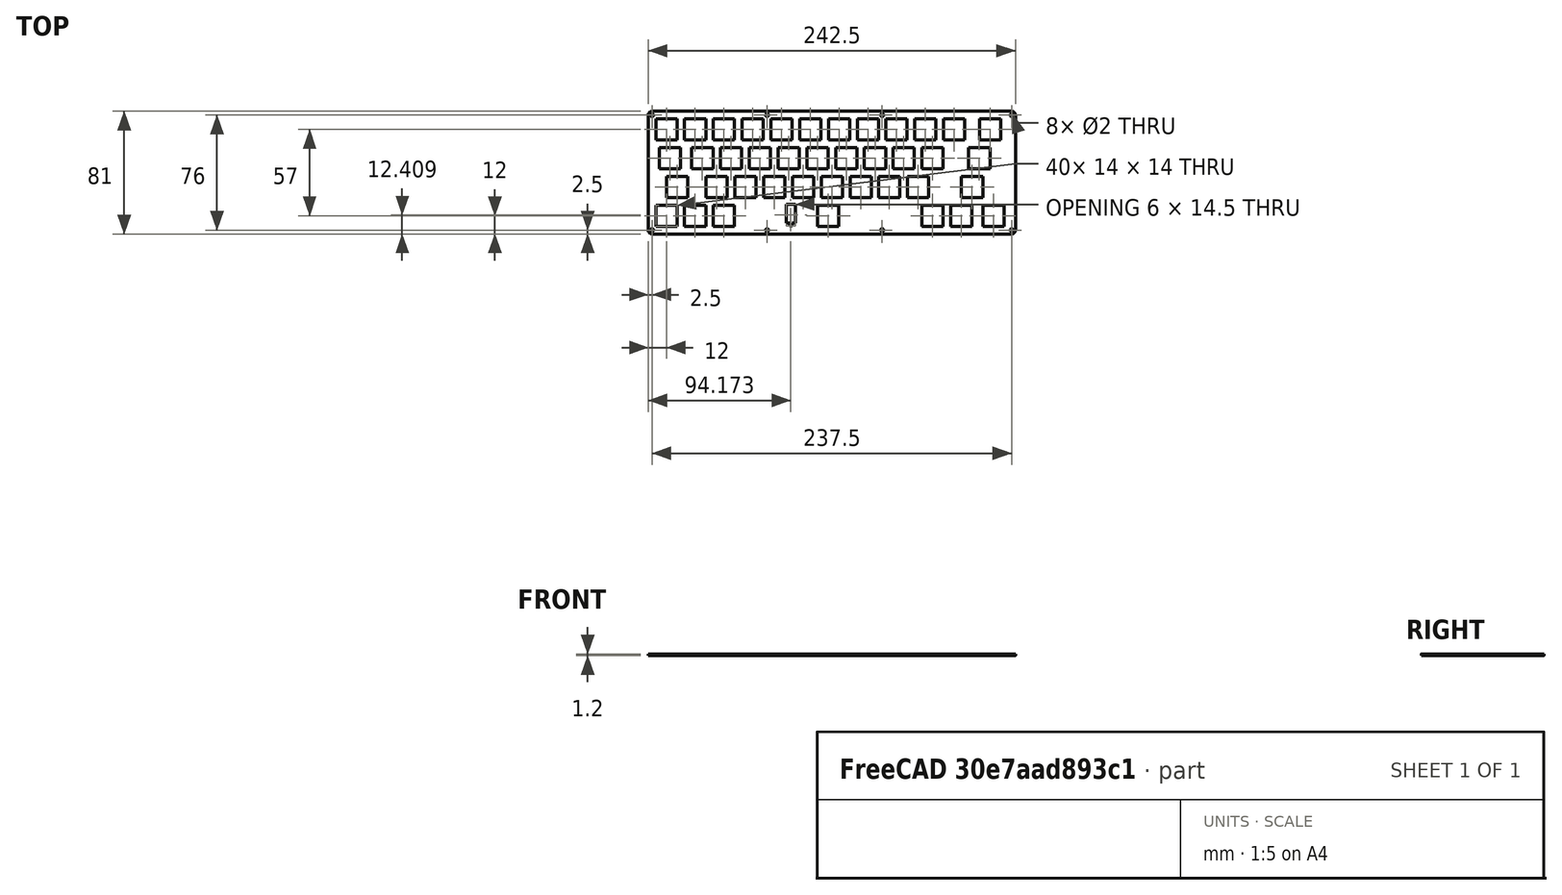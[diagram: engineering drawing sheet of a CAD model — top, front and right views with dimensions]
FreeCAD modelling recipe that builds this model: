
FCSTD DOCUMENT  (FreeCAD 1.0R39285 (Git))
Label: keys-plate
License: All rights reserved
LicenseURL: https://en.wikipedia.org/wiki/All_rights_reserved
objects: Sketcher::SketchObject×2, PartDesign::Pad×1, PartDesign::Body×1
note: 8 computed .brp shape members not serialized (recipe doc carries the construction recipe); baked Part::Feature solids carry a one-line shape summary decoded from their .brp

FEATURE [Sketcher::SketchObject] Sketch
  ArcFitTolerance = 1e-06
  FullyConstrained = true
  MakeInternals = false
FEATURE [Sketcher::SketchObject] Sketch001
  ArcFitTolerance = 1e-06
  AttachmentSupport = -> [XY_Plane]
  FullyConstrained = false
  MakeInternals = false
  MapMode = 5
  sketch-geometry (184):
    g0: LineSegment StartX=-121.25 StartY=-38 StartZ=0 EndX=-121.25 EndY=38 EndZ=0
    g1: ArcOfCircle CenterX=-118.75 CenterY=38 CenterZ=0 NormalX=0 NormalY=0 NormalZ=1 AngleXU=0 Radius=2.5 StartAngle=1.5708 EndAngle=3.14159
    g2: LineSegment StartX=-118.75 StartY=40.5 StartZ=0 EndX=118.75 EndY=40.5 EndZ=0
    g3: ArcOfCircle CenterX=118.75 CenterY=38 CenterZ=0 NormalX=0 NormalY=0 NormalZ=1 AngleXU=0 Radius=2.5 StartAngle=4e-16 EndAngle=1.5708
    g4: LineSegment StartX=121.25 StartY=38 StartZ=0 EndX=121.25 EndY=-38 EndZ=0
    g5: ArcOfCircle CenterX=118.75 CenterY=-38 CenterZ=0 NormalX=0 NormalY=0 NormalZ=1 AngleXU=0 Radius=2.5 StartAngle=4.71239 EndAngle=6.28319
    g6: LineSegment StartX=118.75 StartY=-40.5 StartZ=0 EndX=-118.75 EndY=-40.5 EndZ=0
    g7: ArcOfCircle CenterX=-118.75 CenterY=-38 CenterZ=0 NormalX=0 NormalY=0 NormalZ=1 AngleXU=0 Radius=2.5 StartAngle=3.14159 EndAngle=4.71239
    g8: Circle CenterX=-118.75 CenterY=38 CenterZ=0 NormalX=0 NormalY=0 NormalZ=1 AngleXU=0 Radius=1
    g9: Circle CenterX=-42.75 CenterY=38 CenterZ=0 NormalX=0 NormalY=0 NormalZ=1 AngleXU=0 Radius=1
    g10: Circle CenterX=33.25 CenterY=38 CenterZ=0 NormalX=0 NormalY=0 NormalZ=1 AngleXU=0 Radius=1
    g11: Circle CenterX=118.75 CenterY=38 CenterZ=0 NormalX=0 NormalY=0 NormalZ=1 AngleXU=0 Radius=1
    g12: Circle CenterX=-118.75 CenterY=-38 CenterZ=0 NormalX=0 NormalY=0 NormalZ=1 AngleXU=0 Radius=1
    g13: Circle CenterX=-42.75 CenterY=-38 CenterZ=0 NormalX=0 NormalY=0 NormalZ=1 AngleXU=0 Radius=1
    g14: Circle CenterX=33.25 CenterY=-38 CenterZ=0 NormalX=0 NormalY=0 NormalZ=1 AngleXU=0 Radius=1
    g15: Circle CenterX=118.75 CenterY=-38 CenterZ=0 NormalX=0 NormalY=0 NormalZ=1 AngleXU=0 Radius=1
    g16: LineSegment StartX=-116.25 StartY=35.5 StartZ=0 EndX=-116.25 EndY=21.5 EndZ=0
    g17: LineSegment StartX=-116.25 StartY=21.5 StartZ=0 EndX=-102.25 EndY=21.5 EndZ=0
    g18: LineSegment StartX=-102.25 StartY=21.5 StartZ=0 EndX=-102.25 EndY=35.5 EndZ=0
    g19: LineSegment StartX=-102.25 StartY=35.5 StartZ=0 EndX=-116.25 EndY=35.5 EndZ=0
    g20: LineSegment StartX=35.75 StartY=35.5 StartZ=0 EndX=35.75 EndY=21.5 EndZ=0
    g21: LineSegment StartX=35.75 StartY=21.5 StartZ=0 EndX=49.75 EndY=21.5 EndZ=0
    g22: LineSegment StartX=49.75 StartY=21.5 StartZ=0 EndX=49.75 EndY=35.5 EndZ=0
    g23: LineSegment StartX=49.75 StartY=35.5 StartZ=0 EndX=35.75 EndY=35.5 EndZ=0
    g24: LineSegment StartX=-97.25 StartY=35.5 StartZ=0 EndX=-97.25 EndY=21.5 EndZ=0
    g25: LineSegment StartX=-97.25 StartY=21.5 StartZ=0 EndX=-83.25 EndY=21.5 EndZ=0
    g26: LineSegment StartX=-83.25 StartY=21.5 StartZ=0 EndX=-83.25 EndY=35.5 EndZ=0
    g27: LineSegment StartX=-83.25 StartY=35.5 StartZ=0 EndX=-97.25 EndY=35.5 EndZ=0
    g28: LineSegment StartX=16.75 StartY=35.5 StartZ=0 EndX=16.75 EndY=21.5 EndZ=0
    g29: LineSegment StartX=16.75 StartY=21.5 StartZ=0 EndX=30.75 EndY=21.5 EndZ=0
    g30: LineSegment StartX=30.75 StartY=21.5 StartZ=0 EndX=30.75 EndY=35.5 EndZ=0
    g31: LineSegment StartX=30.75 StartY=35.5 StartZ=0 EndX=16.75 EndY=35.5 EndZ=0
    g32: LineSegment StartX=-2.25 StartY=35.5 StartZ=0 EndX=-2.25 EndY=21.5 EndZ=0
    g33: LineSegment StartX=-2.25 StartY=21.5 StartZ=0 EndX=11.75 EndY=21.5 EndZ=0
    g34: LineSegment StartX=11.75 StartY=21.5 StartZ=0 EndX=11.75 EndY=35.5 EndZ=0
    g35: LineSegment StartX=11.75 StartY=35.5 StartZ=0 EndX=-2.25 EndY=35.5 EndZ=0
    g36: LineSegment StartX=-21.25 StartY=35.5 StartZ=0 EndX=-21.25 EndY=21.5 EndZ=0
    g37: LineSegment StartX=-21.25 StartY=21.5 StartZ=0 EndX=-7.25 EndY=21.5 EndZ=0
    g38: LineSegment StartX=-7.25 StartY=21.5 StartZ=0 EndX=-7.25 EndY=35.5 EndZ=0
    g39: LineSegment StartX=-7.25 StartY=35.5 StartZ=0 EndX=-21.25 EndY=35.5 EndZ=0
    g40: LineSegment StartX=-40.25 StartY=35.5 StartZ=0 EndX=-40.25 EndY=21.5 EndZ=0
    g41: LineSegment StartX=-40.25 StartY=21.5 StartZ=0 EndX=-26.25 EndY=21.5 EndZ=0
    g42: LineSegment StartX=-26.25 StartY=21.5 StartZ=0 EndX=-26.25 EndY=35.5 EndZ=0
    g43: LineSegment StartX=-26.25 StartY=35.5 StartZ=0 EndX=-40.25 EndY=35.5 EndZ=0
    g44: LineSegment StartX=-78.25 StartY=35.5 StartZ=0 EndX=-78.25 EndY=21.5 EndZ=0
    g45: LineSegment StartX=-78.25 StartY=21.5 StartZ=0 EndX=-64.25 EndY=21.5 EndZ=0
    g46: LineSegment StartX=-64.25 StartY=21.5 StartZ=0 EndX=-64.25 EndY=35.5 EndZ=0
    g47: LineSegment StartX=-64.25 StartY=35.5 StartZ=0 EndX=-78.25 EndY=35.5 EndZ=0
    g48: LineSegment StartX=-59.25 StartY=35.5 StartZ=0 EndX=-59.25 EndY=21.5 EndZ=0
    g49: LineSegment StartX=-59.25 StartY=21.5 StartZ=0 EndX=-45.25 EndY=21.5 EndZ=0
    g50: LineSegment StartX=-45.25 StartY=21.5 StartZ=0 EndX=-45.25 EndY=35.5 EndZ=0
    g51: LineSegment StartX=-45.25 StartY=35.5 StartZ=0 EndX=-59.25 EndY=35.5 EndZ=0
    g52: LineSegment StartX=73.75 StartY=35.5 StartZ=0 EndX=73.75 EndY=21.5 EndZ=0
    g53: LineSegment StartX=73.75 StartY=21.5 StartZ=0 EndX=87.75 EndY=21.5 EndZ=0
    g54: LineSegment StartX=87.75 StartY=21.5 StartZ=0 EndX=87.75 EndY=35.5 EndZ=0
    g55: LineSegment StartX=87.75 StartY=35.5 StartZ=0 EndX=73.75 EndY=35.5 EndZ=0
    g56: LineSegment StartX=-92.5 StartY=16.5 StartZ=0 EndX=-92.5 EndY=2.5 EndZ=0
    g57: LineSegment StartX=-92.5 StartY=2.5 StartZ=0 EndX=-78.5 EndY=2.5 EndZ=0
    g58: LineSegment StartX=-78.5 StartY=2.5 StartZ=0 EndX=-78.5 EndY=16.5 EndZ=0
    g59: LineSegment StartX=-78.5 StartY=16.5 StartZ=0 EndX=-92.5 EndY=16.5 EndZ=0
    g60: LineSegment StartX=54.75 StartY=35.5 StartZ=0 EndX=54.75 EndY=21.5 EndZ=0
    g61: LineSegment StartX=54.75 StartY=21.5 StartZ=0 EndX=68.75 EndY=21.5 EndZ=0
    g62: LineSegment StartX=68.75 StartY=21.5 StartZ=0 EndX=68.75 EndY=35.5 EndZ=0
    g63: LineSegment StartX=68.75 StartY=35.5 StartZ=0 EndX=54.75 EndY=35.5 EndZ=0
    g64: LineSegment StartX=-113.875 StartY=16.5 StartZ=0 EndX=-113.875 EndY=2.5 EndZ=0
    g65: LineSegment StartX=-113.875 StartY=2.5 StartZ=0 EndX=-99.875 EndY=2.5 EndZ=0
    g66: LineSegment StartX=-99.875 StartY=2.5 StartZ=0 EndX=-99.875 EndY=16.5 EndZ=0
    g67: LineSegment StartX=-99.875 StartY=16.5 StartZ=0 EndX=-113.875 EndY=16.5 EndZ=0
    g68: LineSegment StartX=97.5 StartY=35.5 StartZ=0 EndX=97.5 EndY=21.5 EndZ=0
    g69: LineSegment StartX=97.5 StartY=21.5 StartZ=0 EndX=111.5 EndY=21.5 EndZ=0
    g70: LineSegment StartX=111.5 StartY=21.5 StartZ=0 EndX=111.5 EndY=35.5 EndZ=0
    g71: LineSegment StartX=111.5 StartY=35.5 StartZ=0 EndX=97.5 EndY=35.5 EndZ=0
    g72: LineSegment StartX=-73.5 StartY=16.5 StartZ=0 EndX=-73.5 EndY=2.5 EndZ=0
    g73: LineSegment StartX=-73.5 StartY=2.5 StartZ=0 EndX=-59.5 EndY=2.5 EndZ=0
    g74: LineSegment StartX=-59.5 StartY=2.5 StartZ=0 EndX=-59.5 EndY=16.5 EndZ=0
    g75: LineSegment StartX=-59.5 StartY=16.5 StartZ=0 EndX=-73.5 EndY=16.5 EndZ=0
    g76: LineSegment StartX=2.5 StartY=16.5 StartZ=0 EndX=2.5 EndY=2.5 EndZ=0
    g77: LineSegment StartX=2.5 StartY=2.5 StartZ=0 EndX=16.5 EndY=2.5 EndZ=0
    g78: LineSegment StartX=16.5 StartY=2.5 StartZ=0 EndX=16.5 EndY=16.5 EndZ=0
    g79: LineSegment StartX=16.5 StartY=16.5 StartZ=0 EndX=2.5 EndY=16.5 EndZ=0
    g80: LineSegment StartX=-54.5 StartY=16.5 StartZ=0 EndX=-54.5 EndY=2.5 EndZ=0
    g81: LineSegment StartX=-54.5 StartY=2.5 StartZ=0 EndX=-40.5 EndY=2.5 EndZ=0
    g82: LineSegment StartX=-40.5 StartY=2.5 StartZ=0 EndX=-40.5 EndY=16.5 EndZ=0
    g83: LineSegment StartX=-40.5 StartY=16.5 StartZ=0 EndX=-54.5 EndY=16.5 EndZ=0
    g84: LineSegment StartX=40.5 StartY=16.5 StartZ=0 EndX=40.5 EndY=2.5 EndZ=0
    g85: LineSegment StartX=40.5 StartY=2.5 StartZ=0 EndX=54.5 EndY=2.5 EndZ=0
    g86: LineSegment StartX=54.5 StartY=2.5 StartZ=0 EndX=54.5 EndY=16.5 EndZ=0
    g87: LineSegment StartX=54.5 StartY=16.5 StartZ=0 EndX=40.5 EndY=16.5 EndZ=0
    g88: LineSegment StartX=-35.5 StartY=16.5 StartZ=0 EndX=-35.5 EndY=2.5 EndZ=0
    g89: LineSegment StartX=-35.5 StartY=2.5 StartZ=0 EndX=-21.5 EndY=2.5 EndZ=0
    g90: LineSegment StartX=-21.5 StartY=2.5 StartZ=0 EndX=-21.5 EndY=16.5 EndZ=0
    g91: LineSegment StartX=-21.5 StartY=16.5 StartZ=0 EndX=-35.5 EndY=16.5 EndZ=0
    g92: LineSegment StartX=21.5 StartY=16.5 StartZ=0 EndX=21.5 EndY=2.5 EndZ=0
    g93: LineSegment StartX=21.5 StartY=2.5 StartZ=0 EndX=35.5 EndY=2.5 EndZ=0
    g94: LineSegment StartX=35.5 StartY=2.5 StartZ=0 EndX=35.5 EndY=16.5 EndZ=0
    g95: LineSegment StartX=35.5 StartY=16.5 StartZ=0 EndX=21.5 EndY=16.5 EndZ=0
    g96: LineSegment StartX=90.375 StartY=16.5 StartZ=0 EndX=90.375 EndY=2.5 EndZ=0
    g97: LineSegment StartX=90.375 StartY=2.5 StartZ=0 EndX=104.375 EndY=2.5 EndZ=0
    g98: LineSegment StartX=104.375 StartY=2.5 StartZ=0 EndX=104.375 EndY=16.5 EndZ=0
    g99: LineSegment StartX=104.375 StartY=16.5 StartZ=0 EndX=90.375 EndY=16.5 EndZ=0
    g100: LineSegment StartX=-109.125 StartY=-2.5 StartZ=0 EndX=-109.125 EndY=-16.5 EndZ=0
    g101: LineSegment StartX=-109.125 StartY=-16.5 StartZ=0 EndX=-95.125 EndY=-16.5 EndZ=0
    g102: LineSegment StartX=-95.125 StartY=-16.5 StartZ=0 EndX=-95.125 EndY=-2.5 EndZ=0
    g103: LineSegment StartX=-95.125 StartY=-2.5 StartZ=0 EndX=-109.125 EndY=-2.5 EndZ=0
    g104: LineSegment StartX=59.5 StartY=16.5 StartZ=0 EndX=59.5 EndY=2.5 EndZ=0
    g105: LineSegment StartX=59.5 StartY=2.5 StartZ=0 EndX=73.5 EndY=2.5 EndZ=0
    g106: LineSegment StartX=73.5 StartY=2.5 StartZ=0 EndX=73.5 EndY=16.5 EndZ=0
    g107: LineSegment StartX=73.5 StartY=16.5 StartZ=0 EndX=59.5 EndY=16.5 EndZ=0
    g108: LineSegment StartX=-116.25 StartY=-21.5 StartZ=0 EndX=-116.25 EndY=-35.5 EndZ=0
    g109: LineSegment StartX=-116.25 StartY=-35.5 StartZ=0 EndX=-102.25 EndY=-35.5 EndZ=0
    g110: LineSegment StartX=-102.25 StartY=-35.5 StartZ=0 EndX=-102.25 EndY=-21.5 EndZ=0
    g111: LineSegment StartX=-102.25 StartY=-21.5 StartZ=0 EndX=-116.25 EndY=-21.5 EndZ=0
    g112: LineSegment StartX=-83 StartY=-2.5 StartZ=0 EndX=-83 EndY=-16.5 EndZ=0
    g113: LineSegment StartX=-83 StartY=-16.5 StartZ=0 EndX=-69 EndY=-16.5 EndZ=0
    g114: LineSegment StartX=-69 StartY=-16.5 StartZ=0 EndX=-69 EndY=-2.5 EndZ=0
    g115: LineSegment StartX=-69 StartY=-2.5 StartZ=0 EndX=-83 EndY=-2.5 EndZ=0
    g116: LineSegment StartX=-64 StartY=-2.5 StartZ=0 EndX=-64 EndY=-16.5 EndZ=0
    g117: LineSegment StartX=-64 StartY=-16.5 StartZ=0 EndX=-50 EndY=-16.5 EndZ=0
    g118: LineSegment StartX=-50 StartY=-16.5 StartZ=0 EndX=-50 EndY=-2.5 EndZ=0
    g119: LineSegment StartX=-50 StartY=-2.5 StartZ=0 EndX=-64 EndY=-2.5 EndZ=0
    g120: LineSegment StartX=-45 StartY=-2.5 StartZ=0 EndX=-45 EndY=-16.5 EndZ=0
    g121: LineSegment StartX=-45 StartY=-16.5 StartZ=0 EndX=-31 EndY=-16.5 EndZ=0
    g122: LineSegment StartX=-31 StartY=-16.5 StartZ=0 EndX=-31 EndY=-2.5 EndZ=0
    g123: LineSegment StartX=-31 StartY=-2.5 StartZ=0 EndX=-45 EndY=-2.5 EndZ=0
    g124: LineSegment StartX=-97.25 StartY=-21.5 StartZ=0 EndX=-97.25 EndY=-35.5 EndZ=0
    g125: LineSegment StartX=-97.25 StartY=-35.5 StartZ=0 EndX=-83.25 EndY=-35.5 EndZ=0
    g126: LineSegment StartX=-83.25 StartY=-35.5 StartZ=0 EndX=-83.25 EndY=-21.5 EndZ=0
    g127: LineSegment StartX=-83.25 StartY=-21.5 StartZ=0 EndX=-97.25 EndY=-21.5 EndZ=0
    g128: LineSegment StartX=-78.25 StartY=-21.5 StartZ=0 EndX=-78.25 EndY=-35.5 EndZ=0
    g129: LineSegment StartX=-78.25 StartY=-35.5 StartZ=0 EndX=-64.25 EndY=-35.5 EndZ=0
    g130: LineSegment StartX=-64.25 StartY=-35.5 StartZ=0 EndX=-64.25 EndY=-21.5 EndZ=0
    g131: LineSegment StartX=-64.25 StartY=-21.5 StartZ=0 EndX=-78.25 EndY=-21.5 EndZ=0
    g132: LineSegment StartX=-26 StartY=-2.5 StartZ=0 EndX=-26 EndY=-16.5 EndZ=0
    g133: LineSegment StartX=-26 StartY=-16.5 StartZ=0 EndX=-12 EndY=-16.5 EndZ=0
    g134: LineSegment StartX=-12 StartY=-16.5 StartZ=0 EndX=-12 EndY=-2.5 EndZ=0
    g135: LineSegment StartX=-12 StartY=-2.5 StartZ=0 EndX=-26 EndY=-2.5 EndZ=0
    g136: LineSegment StartX=-9.375 StartY=-21.5 StartZ=0 EndX=-9.375 EndY=-35.5 EndZ=0
    g137: LineSegment StartX=-9.375 StartY=-35.5 StartZ=0 EndX=4.625 EndY=-35.5 EndZ=0
    g138: LineSegment StartX=4.625 StartY=-35.5 StartZ=0 EndX=4.625 EndY=-21.5 EndZ=0
    g139: LineSegment StartX=4.625 StartY=-21.5 StartZ=0 EndX=-9.375 EndY=-21.5 EndZ=0
    g140: LineSegment StartX=-7 StartY=-2.5 StartZ=0 EndX=-7 EndY=-16.5 EndZ=0
    g141: LineSegment StartX=-7 StartY=-16.5 StartZ=0 EndX=7 EndY=-16.5 EndZ=0
    g142: LineSegment StartX=7 StartY=-16.5 StartZ=0 EndX=7 EndY=-2.5 EndZ=0
    g143: LineSegment StartX=7 StartY=-2.5 StartZ=0 EndX=-7 EndY=-2.5 EndZ=0
    g144: LineSegment StartX=12 StartY=-2.5 StartZ=0 EndX=12 EndY=-16.5 EndZ=0
    g145: LineSegment StartX=12 StartY=-16.5 StartZ=0 EndX=26 EndY=-16.5 EndZ=0
    g146: LineSegment StartX=26 StartY=-16.5 StartZ=0 EndX=26 EndY=-2.5 EndZ=0
    g147: LineSegment StartX=26 StartY=-2.5 StartZ=0 EndX=12 EndY=-2.5 EndZ=0
    g148: LineSegment StartX=59.5 StartY=-21.5 StartZ=0 EndX=59.5 EndY=-35.5 EndZ=0
    g149: LineSegment StartX=59.5 StartY=-35.5 StartZ=0 EndX=73.5 EndY=-35.5 EndZ=0
    g150: LineSegment StartX=73.5 StartY=-35.5 StartZ=0 EndX=73.5 EndY=-21.5 EndZ=0
    g151: LineSegment StartX=73.5 StartY=-21.5 StartZ=0 EndX=59.5 EndY=-21.5 EndZ=0
    g152: LineSegment StartX=-16.5 StartY=16.5 StartZ=0 EndX=-16.5 EndY=2.5 EndZ=0
    g153: LineSegment StartX=-16.5 StartY=2.5 StartZ=0 EndX=-2.5 EndY=2.5 EndZ=0
    g154: LineSegment StartX=-2.5 StartY=2.5 StartZ=0 EndX=-2.5 EndY=16.5 EndZ=0
    g155: LineSegment StartX=-2.5 StartY=16.5 StartZ=0 EndX=-16.5 EndY=16.5 EndZ=0
    g156: LineSegment StartX=31 StartY=-2.5 StartZ=0 EndX=31 EndY=-16.5 EndZ=0
    g157: LineSegment StartX=31 StartY=-16.5 StartZ=0 EndX=45 EndY=-16.5 EndZ=0
    g158: LineSegment StartX=45 StartY=-16.5 StartZ=0 EndX=45 EndY=-2.5 EndZ=0
    g159: LineSegment StartX=45 StartY=-2.5 StartZ=0 EndX=31 EndY=-2.5 EndZ=0
    g160: LineSegment StartX=50 StartY=-2.5 StartZ=0 EndX=50 EndY=-16.5 EndZ=0
    g161: LineSegment StartX=50 StartY=-16.5 StartZ=0 EndX=64 EndY=-16.5 EndZ=0
    g162: LineSegment StartX=64 StartY=-16.5 StartZ=0 EndX=64 EndY=-2.5 EndZ=0
    g163: LineSegment StartX=64 StartY=-2.5 StartZ=0 EndX=50 EndY=-2.5 EndZ=0
    g164: LineSegment StartX=85.625 StartY=-2.5 StartZ=0 EndX=85.625 EndY=-16.5 EndZ=0
    g165: LineSegment StartX=85.625 StartY=-16.5 StartZ=0 EndX=99.625 EndY=-16.5 EndZ=0
    g166: LineSegment StartX=99.625 StartY=-16.5 StartZ=0 EndX=99.625 EndY=-2.5 EndZ=0
    g167: LineSegment StartX=99.625 StartY=-2.5 StartZ=0 EndX=85.625 EndY=-2.5 EndZ=0
    g168: LineSegment StartX=78.5 StartY=-21.5 StartZ=0 EndX=78.5 EndY=-35.5 EndZ=0
    g169: LineSegment StartX=78.5 StartY=-35.5 StartZ=0 EndX=92.5 EndY=-35.5 EndZ=0
    g170: LineSegment StartX=92.5 StartY=-35.5 StartZ=0 EndX=92.5 EndY=-21.5 EndZ=0
    g171: LineSegment StartX=92.5 StartY=-21.5 StartZ=0 EndX=78.5 EndY=-21.5 EndZ=0
    g172: LineSegment StartX=99.875 StartY=-21.5 StartZ=0 EndX=99.875 EndY=-35.5 EndZ=0
    g173: LineSegment StartX=99.875 StartY=-35.5 StartZ=0 EndX=113.875 EndY=-35.5 EndZ=0
    g174: LineSegment StartX=113.875 StartY=-35.5 StartZ=0 EndX=113.875 EndY=-21.5 EndZ=0
    g175: LineSegment StartX=113.875 StartY=-21.5 StartZ=0 EndX=99.875 EndY=-21.5 EndZ=0
    g176: LineSegment StartX=-30.0771 StartY=-20.9555 StartZ=0 EndX=-24.0771 EndY=-20.9555 EndZ=0
    g177: LineSegment StartX=-24.0771 StartY=-20.9555 StartZ=0 EndX=-24.0771 EndY=-33.4555 EndZ=0
    g178: LineSegment StartX=-24.0771 StartY=-33.4555 StartZ=0 EndX=-26.2271 EndY=-33.4555 EndZ=0
    g179: LineSegment StartX=-26.2271 StartY=-33.4555 StartZ=0 EndX=-26.2271 EndY=-34.9555 EndZ=0
    g180: LineSegment StartX=-26.2271 StartY=-34.9555 StartZ=0 EndX=-27.9271 EndY=-34.9555 EndZ=0
    g181: LineSegment StartX=-27.9271 StartY=-34.9555 StartZ=0 EndX=-27.9271 EndY=-33.4555 EndZ=0
    g182: LineSegment StartX=-27.9271 StartY=-33.4555 StartZ=0 EndX=-30.0771 EndY=-33.4555 EndZ=0
    g183: LineSegment StartX=-30.0771 StartY=-33.4555 StartZ=0 EndX=-30.0771 EndY=-20.9555 EndZ=0
  constraints (545):
    c: Tangent(g0,g1) = 1.5708
    c: Tangent(g1,g2) = 1.5708
    c: Tangent(g2,g3) = 1.5708
    c: Tangent(g3,g4) = 1.5708
    c: Tangent(g4,g5) = 1.5708
    c: Tangent(g5,g6) = 1.5708
    c: Tangent(g6,g7) = 1.5708
    c: Tangent(g7,g0) = 1.5708
    c: Vertical(g0)
    c: Vertical(g4)
    c: Horizontal(g2)
    c: Horizontal(g6)
    c: Radius(g1) = 2.5
    c: Radius(g3) = 2.5
    c: Radius(g5) = 2.5
    c: Radius(g7) = 2.5
    c: Symmetric(g1,g5,g-1)
    c: Distance(g4,g0) = 242.5
    c: Distance(g6,g2) = 81
    c: Diameter(g8) = 2
    c: Diameter(g9) = 2
    c: Diameter(g10) = 2
    c: Diameter(g11) = 2
    c: Diameter(g12) = 2
    c: Diameter(g13) = 2
    c: Diameter(g14) = 2
    c: Diameter(g15) = 2
    c: Distance(g12,g0) = 2.5
    c: Distance(g15,g4) = 2.5
    c: Horizontal(g7,g13)
    c: Horizontal(g13,g14)
    c: Horizontal(g15,g14)
    c: Vertical(g11,g5)
    c: Vertical(g7,g8)
    c: Distance(g8,g6) = 78.5
    c: Vertical(g9,g13)
    c: Horizontal(g8,g9)
    c: Horizontal(g10,g9)
    c: Horizontal(g11,g10)
    c: Vertical(g10,g14)
    c: Distance(g14,g4) = 88
    c: Distance(g13,g0) = 78.5  'h0l1_14_h'
    c: Distance(g12,g6) = 2.5
    c: Coincident(g16,g17)
    c: Coincident(g17,g18)
    c: Coincident(g18,g19)
    c: Coincident(g19,g16)
    c: Vertical(g16)
    c: DistanceX(g19,g19) = 14
    c: Perpendicular(g16,g19)
    c: Equal(g16,g19)
    c: Equal(g19,g18)
    c: Equal(g18,g17)
    c: Coincident(g20,g21)
    c: Coincident(g21,g22)
    c: Coincident(g22,g23)
    c: Coincident(g23,g20)
    c: Vertical(g20)
    c: DistanceX(g23,g23) = 14
    c: Perpendicular(g20,g23)
    c: Equal(g20,g23)
    c: Equal(g23,g22)
    c: Equal(g22,g21)
    c: Coincident(g24,g25)
    c: Coincident(g25,g26)
    c: Coincident(g26,g27)
    c: Coincident(g27,g24)
    c: Vertical(g24)
    c: DistanceX(g27,g27) = 14
    c: Perpendicular(g24,g27)
    c: Equal(g24,g27)
    c: Equal(g27,g26)
    c: Equal(g26,g25)
    c: Distance(g2,g19) = 5
    c: Distance(g27,g2) = 5
    c: Distance(g24,g18) = 5
    c: Coincident(g28,g29)
    c: Coincident(g29,g30)
    c: Coincident(g30,g31)
    c: Coincident(g31,g28)
    c: Vertical(g28)
    c: DistanceX(g31,g31) = 14
    c: Perpendicular(g28,g31)
    c: Equal(g28,g31)
    c: Equal(g31,g30)
    c: Equal(g30,g29)
    c: Coincident(g32,g33)
    c: Coincident(g33,g34)
    c: Coincident(g34,g35)
    c: Coincident(g35,g32)
    c: Vertical(g32)
    c: DistanceX(g35,g35) = 14
    c: Perpendicular(g32,g35)
    c: Equal(g32,g35)
    c: Equal(g35,g34)
    c: Equal(g34,g33)
    c: Coincident(g36,g37)
    c: Coincident(g37,g38)
    c: Coincident(g38,g39)
    c: Coincident(g39,g36)
    c: Vertical(g36)
    c: DistanceX(g39,g39) = 14
    c: Perpendicular(g36,g39)
    c: Equal(g36,g39)
    c: Equal(g39,g38)
    c: Equal(g38,g37)
    c: Coincident(g40,g41)
    c: Coincident(g41,g42)
    c: Coincident(g42,g43)
    c: Coincident(g43,g40)
    c: Vertical(g40)
    c: DistanceX(g43,g43) = 14
    c: Perpendicular(g40,g43)
    c: Equal(g40,g43)
    c: Equal(g43,g42)
    c: Equal(g42,g41)
    c: Coincident(g44,g45)
    c: Coincident(g45,g46)
    c: Coincident(g46,g47)
    c: Coincident(g47,g44)
    c: Vertical(g44)
    c: DistanceX(g47,g47) = 14
    c: Perpendicular(g44,g47)
    c: Equal(g44,g47)
    c: Equal(g47,g46)
    c: Equal(g46,g45)
    c: Coincident(g48,g49)
    c: Coincident(g49,g50)
    c: Coincident(g50,g51)
    c: Coincident(g51,g48)
    c: Vertical(g48)
    c: DistanceX(g51,g51) = 14
    c: Perpendicular(g48,g51)
    c: Equal(g48,g51)
    c: Equal(g51,g50)
    c: Equal(g50,g49)
    c: Distance(g51,g2) = 5
    c: Distance(g46,g48) = 5
    c: Distance(g2,g43) = 5
    c: Distance(g50,g40) = 5
    c: Distance(g26,g44) = 5
    c: Distance(g2,g47) = 5
    c: Distance(g42,g36) = 5
    c: Distance(g32,g38) = 5
    c: Coincident(g52,g53)
    c: Coincident(g53,g54)
    c: Coincident(g54,g55)
    c: Coincident(g55,g52)
    c: Vertical(g52)
    c: DistanceX(g55,g55) = 14
    c: Perpendicular(g52,g55)
    c: Equal(g52,g55)
    c: Equal(g55,g54)
    c: Equal(g54,g53)
    c: Distance(g0,g16) = 5
    c: Distance(g28,g34) = 5
    c: Distance(g30,g20) = 5
    c: Distance(g2,g39) = 5
    c: Distance(g2,g35) = 5
    c: Distance(g31,g2) = 5
    c: Distance(g23,g2) = 5
    c: Distance(g2,g55) = 5
    c: Coincident(g56,g57)
    c: Coincident(g57,g58)
    c: Coincident(g58,g59)
    c: Coincident(g59,g56)
    c: Vertical(g56)
    c: DistanceX(g59,g59) = 14
    c: Perpendicular(g56,g59)
    c: Equal(g56,g59)
    c: Equal(g59,g58)
    c: Equal(g58,g57)
    c: Coincident(g60,g61)
    c: Coincident(g61,g62)
    c: Coincident(g62,g63)
    c: Coincident(g63,g60)
    c: Vertical(g60)
    c: DistanceX(g63,g63) = 14
    c: Perpendicular(g60,g63)
    c: Equal(g60,g63)
    c: Equal(g63,g62)
    c: Equal(g62,g61)
    c: Distance(g60,g22) = 5
    c: Distance(g62,g52) = 5
    c: Distance(g2,g63) = 5
    c: Coincident(g64,g65)
    c: Coincident(g65,g66)
    c: Coincident(g66,g67)
    c: Coincident(g67,g64)
    c: Vertical(g64)
    c: DistanceX(g67,g67) = 14
    c: Perpendicular(g64,g67)
    c: Equal(g64,g67)
    c: Equal(g67,g66)
    c: Equal(g66,g65)
    c: Distance(g0,g64) = 7.375
    c: Distance(g67,g17) = 5
    c: Coincident(g68,g69)
    c: Coincident(g69,g70)
    c: Coincident(g70,g71)
    c: Coincident(g71,g68)
    c: Vertical(g68)
    c: DistanceX(g71,g71) = 14
    c: Perpendicular(g68,g71)
    c: Equal(g68,g71)
    c: Equal(g71,g70)
    c: Equal(g70,g69)
    c: Distance(g2,g71) = 5
    c: Distance(g68,g54) = 9.75
    c: Coincident(g72,g73)
    c: Coincident(g73,g74)
    c: Coincident(g74,g75)
    c: Coincident(g75,g72)
    c: Vertical(g72)
    c: DistanceX(g75,g75) = 14
    c: Perpendicular(g72,g75)
    c: Equal(g72,g75)
    c: Equal(g75,g74)
    c: Equal(g74,g73)
    c: Coincident(g76,g77)
    c: Coincident(g77,g78)
    c: Coincident(g78,g79)
    c: Coincident(g79,g76)
    c: Vertical(g76)
    c: DistanceX(g79,g79) = 14
    c: Perpendicular(g76,g79)
    c: Equal(g76,g79)
    c: Equal(g79,g78)
    c: Equal(g78,g77)
    c: Coincident(g80,g81)
    c: Coincident(g81,g82)
    c: Coincident(g82,g83)
    c: Coincident(g83,g80)
    c: Vertical(g80)
    c: DistanceX(g83,g83) = 14
    c: Perpendicular(g80,g83)
    c: Equal(g80,g83)
    c: Equal(g83,g82)
    c: Equal(g82,g81)
    c: Coincident(g84,g85)
    c: Coincident(g85,g86)
    c: Coincident(g86,g87)
    c: Coincident(g87,g84)
    c: Vertical(g84)
    c: DistanceX(g87,g87) = 14
    c: Perpendicular(g84,g87)
    c: Equal(g84,g87)
    c: Equal(g87,g86)
    c: Equal(g86,g85)
    c: Distance(g56,g66) = 7.375
    c: Distance(g25,g59) = 5
    c: Distance(g58,g72) = 5
    c: Distance(g45,g75) = 5
    c: Coincident(g88,g89)
    c: Coincident(g89,g90)
    c: Coincident(g90,g91)
    c: Coincident(g91,g88)
    c: Vertical(g88)
    c: DistanceX(g91,g91) = 14
    c: Perpendicular(g88,g91)
    c: Equal(g88,g91)
    c: Equal(g91,g90)
    c: Equal(g90,g89)
    c: Coincident(g92,g93)
    c: Coincident(g93,g94)
    c: Coincident(g94,g95)
    c: Coincident(g95,g92)
    c: Vertical(g92)
    c: DistanceX(g95,g95) = 14
    c: Perpendicular(g92,g95)
    c: Equal(g92,g95)
    c: Equal(g95,g94)
    c: Equal(g94,g93)
    c: Coincident(g96,g97)
    c: Coincident(g97,g98)
    c: Coincident(g98,g99)
    c: Coincident(g99,g96)
    c: Vertical(g96)
    c: DistanceX(g99,g99) = 14
    c: Perpendicular(g96,g99)
    c: Equal(g96,g99)
    c: Equal(g99,g98)
    c: Equal(g98,g97)
    c: Distance(g80,g74) = 5
    c: Distance(g49,g83) = 5
    c: Distance(g82,g88) = 5
    c: Distance(g41,g91) = 5
    c: Distance(g33,g79) = 5
    c: Coincident(g100,g101)
    c: Coincident(g101,g102)
    c: Coincident(g102,g103)
    c: Coincident(g103,g100)
    c: Vertical(g100)
    c: DistanceX(g103,g103) = 14
    c: Perpendicular(g100,g103)
    c: Equal(g100,g103)
    c: Equal(g103,g102)
    c: Equal(g102,g101)
    c: Coincident(g104,g105)
    c: Coincident(g105,g106)
    c: Coincident(g106,g107)
    c: Coincident(g107,g104)
    c: Vertical(g104)
    c: DistanceX(g107,g107) = 14
    c: Perpendicular(g104,g107)
    c: Equal(g104,g107)
    c: Equal(g107,g106)
    c: Equal(g106,g105)
    c: Coincident(g108,g109)
    c: Coincident(g109,g110)
    c: Coincident(g110,g111)
    c: Coincident(g111,g108)
    c: Vertical(g108)
    c: DistanceX(g111,g111) = 14
    c: Perpendicular(g108,g111)
    c: Equal(g108,g111)
    c: Equal(g111,g110)
    c: Equal(g110,g109)
    c: Distance(g78,g92) = 5
    c: Distance(g29,g95) = 5
    c: Distance(g94,g84) = 5
    c: Distance(g86,g104) = 5
    c: Distance(g21,g87) = 5
    c: Distance(g61,g107) = 5
    c: Distance(g69,g99) = 5
    c: Distance(g96,g106) = 16.875
    c: Coincident(g112,g113)
    c: Coincident(g113,g114)
    c: Coincident(g114,g115)
    c: Coincident(g115,g112)
    c: Vertical(g112)
    c: DistanceX(g115,g115) = 14
    c: Perpendicular(g112,g115)
    c: Equal(g112,g115)
    c: Equal(g115,g114)
    c: Equal(g114,g113)
    c: Coincident(g116,g117)
    c: Coincident(g117,g118)
    c: Coincident(g118,g119)
    c: Coincident(g119,g116)
    c: Vertical(g116)
    c: DistanceX(g119,g119) = 14
    c: Perpendicular(g116,g119)
    c: Equal(g116,g119)
    c: Equal(g119,g118)
    c: Equal(g118,g117)
    c: Distance(g65,g103) = 5
    c: Distance(g0,g100) = 12.125
    c: Distance(g101,g111) = 5
    c: Distance(g0,g108) = 5
    c: Coincident(g120,g121)
    c: Coincident(g121,g122)
    c: Coincident(g122,g123)
    c: Coincident(g123,g120)
    c: Vertical(g120)
    c: DistanceX(g123,g123) = 14
    c: Perpendicular(g120,g123)
    c: Equal(g120,g123)
    c: Equal(g123,g122)
    c: Equal(g122,g121)
    c: Distance(g57,g115) = 5
    c: Distance(g112,g102) = 12.125
    c: Coincident(g124,g125)
    c: Coincident(g125,g126)
    c: Coincident(g126,g127)
    c: Coincident(g127,g124)
    c: Vertical(g124)
    c: DistanceX(g127,g127) = 14
    c: Perpendicular(g124,g127)
    c: Equal(g124,g127)
    c: Equal(g127,g126)
    c: Equal(g126,g125)
    c: Coincident(g128,g129)
    c: Coincident(g129,g130)
    c: Coincident(g130,g131)
    c: Coincident(g131,g128)
    c: Vertical(g128)
    c: DistanceX(g131,g131) = 14
    c: Perpendicular(g128,g131)
    c: Equal(g128,g131)
    c: Equal(g131,g130)
    c: Equal(g130,g129)
    c: Distance(g101,g127) = 5
    c: Distance(g110,g124) = 5
    c: Distance(g113,g131) = 5
    c: Distance(g126,g128) = 5
    c: Distance(g114,g116) = 5
    c: Distance(g73,g119) = 5
    c: Coincident(g132,g133)
    c: Coincident(g133,g134)
    c: Coincident(g134,g135)
    c: Coincident(g135,g132)
    c: Vertical(g132)
    c: DistanceX(g135,g135) = 14
    c: Perpendicular(g132,g135)
    c: Equal(g132,g135)
    c: Equal(g135,g134)
    c: Equal(g134,g133)
    c: Coincident(g136,g137)
    c: Coincident(g137,g138)
    c: Coincident(g138,g139)
    c: Coincident(g139,g136)
    c: Vertical(g136)
    c: DistanceX(g139,g139) = 14
    c: Perpendicular(g136,g139)
    c: Equal(g136,g139)
    c: Equal(g139,g138)
    c: Equal(g138,g137)
    c: Coincident(g140,g141)
    c: Coincident(g141,g142)
    c: Coincident(g142,g143)
    c: Coincident(g143,g140)
    c: Vertical(g140)
    c: DistanceX(g143,g143) = 14
    c: Perpendicular(g140,g143)
    c: Equal(g140,g143)
    c: Equal(g143,g142)
    c: Equal(g142,g141)
    c: Coincident(g144,g145)
    c: Coincident(g145,g146)
    c: Coincident(g146,g147)
    c: Coincident(g147,g144)
    c: Vertical(g144)
    c: DistanceX(g147,g147) = 14
    c: Perpendicular(g144,g147)
    c: Equal(g144,g147)
    c: Equal(g147,g146)
    c: Equal(g146,g145)
    c: Distance(g118,g120) = 5
    c: Distance(g81,g123) = 5
    c: Distance(g122,g132) = 5
    c: Distance(g89,g135) = 5
    c: Distance(g136,g130) = 54.875
    c: Distance(g134,g140) = 5
    c: Distance(g139,g141) = 5
    c: Coincident(g148,g149)
    c: Coincident(g149,g150)
    c: Coincident(g150,g151)
    c: Coincident(g151,g148)
    c: Vertical(g148)
    c: DistanceX(g151,g151) = 14
    c: Perpendicular(g148,g151)
    c: Equal(g148,g151)
    c: Equal(g151,g150)
    c: Equal(g150,g149)
    c: Coincident(g152,g153)
    c: Coincident(g153,g154)
    c: Coincident(g154,g155)
    c: Coincident(g155,g152)
    c: Vertical(g152)
    c: DistanceX(g155,g155) = 14
    c: Perpendicular(g152,g155)
    c: Equal(g152,g155)
    c: Equal(g155,g154)
    c: Equal(g154,g153)
    c: Coincident(g156,g157)
    c: Coincident(g157,g158)
    c: Coincident(g158,g159)
    c: Coincident(g159,g156)
    c: Vertical(g156)
    c: DistanceX(g159,g159) = 14
    c: Perpendicular(g156,g159)
    c: Equal(g156,g159)
    c: Equal(g159,g158)
    c: Equal(g158,g157)
    c: Coincident(g160,g161)
    c: Coincident(g161,g162)
    c: Coincident(g162,g163)
    c: Coincident(g163,g160)
    c: Vertical(g160)
    c: DistanceX(g163,g163) = 14
    c: Perpendicular(g160,g163)
    c: Equal(g160,g163)
    c: Equal(g163,g162)
    c: Equal(g162,g161)
    c: Coincident(g164,g165)
    c: Coincident(g165,g166)
    c: Coincident(g166,g167)
    c: Coincident(g167,g164)
    c: Vertical(g164)
    c: DistanceX(g167,g167) = 14
    c: Perpendicular(g164,g167)
    c: Equal(g164,g167)
    c: Equal(g167,g166)
    c: Equal(g166,g165)
    c: Distance(g142,g144) = 5
    c: Distance(g148,g138) = 54.875
    c: Distance(g156,g146) = 5
    c: Distance(g160,g158) = 5
    c: Distance(g164,g162) = 21.625
    c: Distance(g97,g167) = 5
    c: Distance(g77,g147) = 5
    c: Coincident(g168,g169)
    c: Coincident(g169,g170)
    c: Coincident(g170,g171)
    c: Coincident(g171,g168)
    c: Vertical(g168)
    c: DistanceX(g171,g171) = 14
    c: Perpendicular(g168,g171)
    c: Equal(g168,g171)
    c: Equal(g171,g170)
    c: Equal(g170,g169)
    c: Coincident(g172,g173)
    c: Coincident(g173,g174)
    c: Coincident(g174,g175)
    c: Coincident(g175,g172)
    c: Vertical(g172)
    c: DistanceX(g175,g175) = 14
    c: Perpendicular(g172,g175)
    c: Equal(g172,g175)
    c: Equal(g175,g174)
    c: Equal(g174,g173)
    c: Distance(g155,g37) = 5
    c: Distance(g143,g153) = 5
    c: Distance(g76,g154) = 5
    c: Distance(g152,g90) = 5
    c: Distance(g159,g85) = 5
    c: Distance(g163,g85) = 5
    c: Distance(g151,g161) = 5
    c: Distance(g150,g168) = 5
    c: Distance(g165,g171) = 5
    c: Distance(g175,g165) = 5
    c: Distance(g172,g170) = 7.375
    c: Horizontal(g176)
    c: Coincident(g176,g177)
    c: Vertical(g177)
    c: Coincident(g177,g178)
    c: Horizontal(g178)
    c: Coincident(g178,g179)
    c: Vertical(g179)
    c: Coincident(g179,g180)
    c: Horizontal(g180)
    c: Coincident(g180,g181)
    c: Vertical(g181)
    c: Coincident(g181,g182)
    c: Horizontal(g182)
    c: Coincident(g182,g183)
    c: Coincident(g183,g176)
    c: Vertical(g183)
    c: Equal(g178,g182)
    c: Distance(g181,g179) = 1.7
    c: Distance(g177,g183) = 6
    c: Distance(g178,g176) = 12.5
    c: Equal(g177,g183)
    c: Distance(g180,g178) = 1.5
FEATURE [PartDesign::Pad] Pad
  Direction = (0,0,1)
  Length = 1.2
  Length2 = 10
  Profile = -> Sketch001
  ReferenceAxis = -> Sketch001 [N_Axis]
  Refine = true
  Suppressed = false
  Type = 0
FEATURE [PartDesign::Body] Body
  AllowCompound = false
  Group = -> [Sketch001,Pad]
  Origin = -> Origin
  Tip = -> Pad
